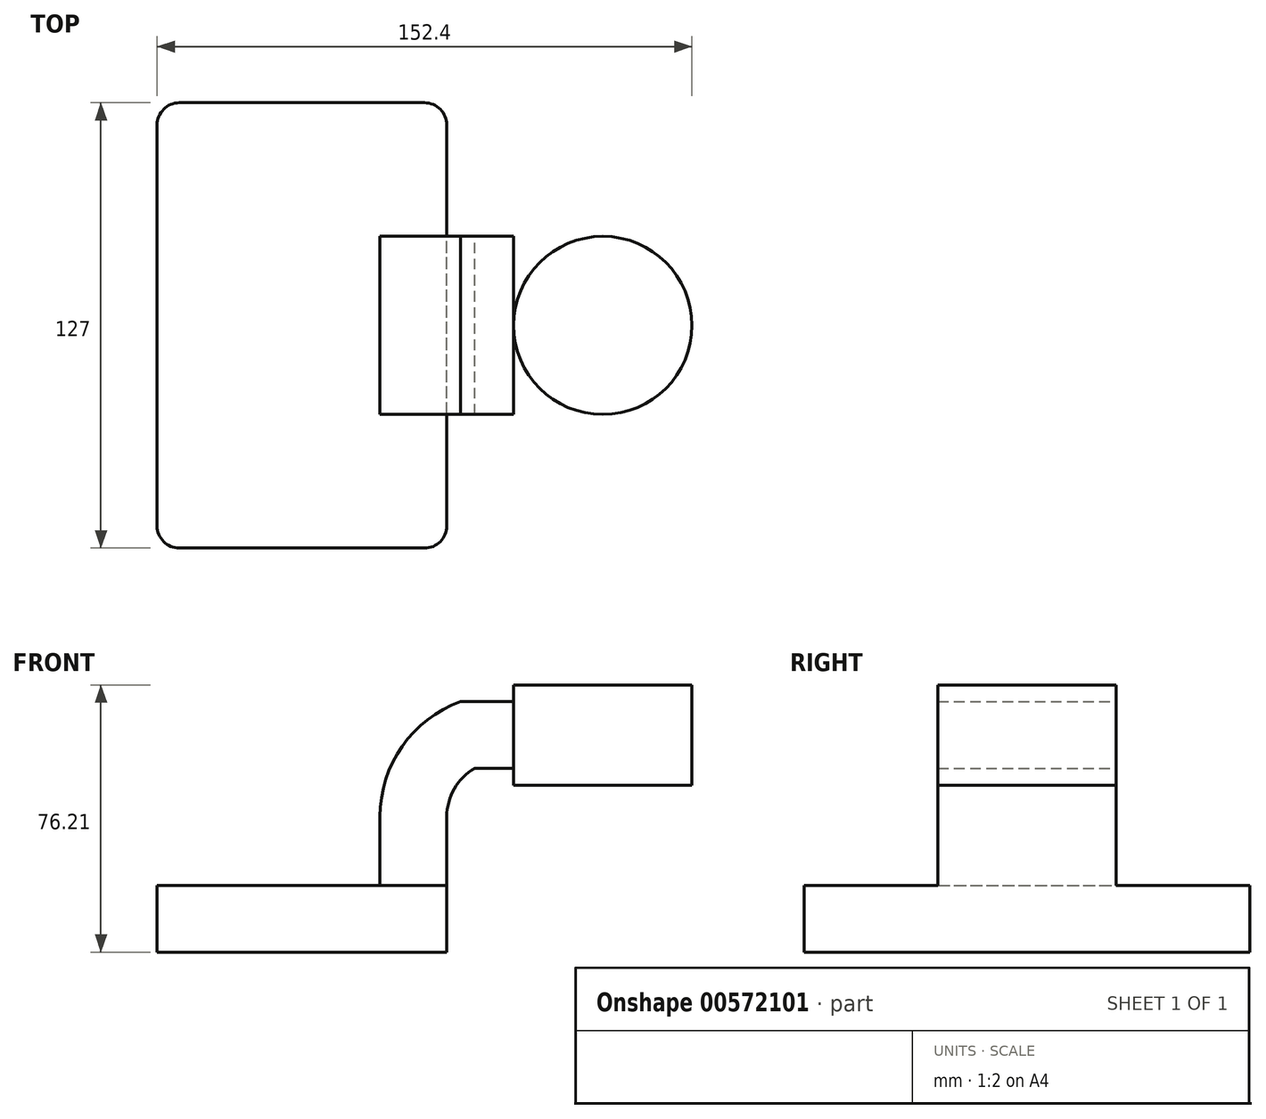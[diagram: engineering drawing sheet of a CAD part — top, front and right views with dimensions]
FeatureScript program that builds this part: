
annotation { "Feature Type Name" : "Feature", "Feature Type Description" : "" }
export const myFeature = defineFeature(function(context is Context, id is Id, definition is map)
    precondition{}
    {
        {
            var Q0;
            Q0=qCreatedBy(makeId("Front.planeOp"),FACE);
            var sketch = newSketch(context, id + "F0", { "sketchPlane" : qUnion([Q0])});
            skLineSegment(sketch, "E0.bottom", {"start": v(41.27, 9.53) * mm, "end": v(-41.28, 9.53) * mm});
            skLineSegment(sketch, "E0.top", {"start": v(41.28, -9.52) * mm, "end": v(-41.27, -9.52) * mm});
            skLineSegment(sketch, "E0.left", {"start": v(41.28, 9.53) * mm, "end": v(41.28, -9.52) * mm});
            skLineSegment(sketch, "E0.right", {"start": v(-41.28, 9.53) * mm, "end": v(-41.27, -9.52) * mm});
            skPoint(sketch, "E0.middle", {"position": v(0, 0) * mm});
            skLineSegment(sketch, "E1.bottom", {"start": v(60.33, 38.1) * mm, "end": v(111.13, 38.1) * mm});
            skLineSegment(sketch, "E1.top", {"start": v(60.33, 66.68) * mm, "end": v(111.12, 66.68) * mm});
            skLineSegment(sketch, "E1.left", {"start": v(60.32, 38.1) * mm, "end": v(60.32, 66.68) * mm});
            skLineSegment(sketch, "E1.right", {"start": v(111.13, 38.1) * mm, "end": v(111.13, 66.68) * mm});
            skPoint(sketch, "E1.middle", {"position": v(85.72, 52.39) * mm});
            skLineSegment(sketch, "E2", {"start": v(41.27, 9.53) * mm, "end": v(41.27, 29.12) * mm});
            skArc(sketch, "E3", {"start": v(41.28, 29.12) * mm, "mid": v(43.4, 37.06) * mm, "end": v(49.22, 42.88) * mm});
            skLineSegment(sketch, "E4", {"start": v(49.22, 42.88) * mm, "end": v(85.72, 42.88) * mm});
            skLineSegment(sketch, "E5.0", {"start": v(45.16, 61.93) * mm, "end": v(85.72, 61.93) * mm});
            skArc(sketch, "E5.1", {"start": v(22.23, 29.12) * mm, "mid": v(28.53, 49.14) * mm, "end": v(45.16, 61.93) * mm});
            skLineSegment(sketch, "E5.2", {"start": v(22.22, 9.53) * mm, "end": v(22.22, 29.12) * mm});
            skLineSegment(sketch, "E6", {"start": v(85.72, 66.68) * mm, "end": v(85.73, 38.1) * mm});
            skFitSpline(sketch, "E7", {"points": [v(-41.28, 9.53) * mm, v(45.16, 61.93) * mm], "startDerivative": vector(0.48, 108.31) * mm, "endDerivative": vector(111.94, 4.14) * mm});
            skSolve(sketch);
        }
        {
            var Q0;
            Q0=makeQuery(id+"F0.imprint","IMPRINT",FACE,{"disambiguationData":[TD([[makeQuery(id+"F0.imprint","IMPRINT",EDGE,{"derivedFrom":sQuery(id+"F0.wireOp",EDGE,"E0.top")}),-1.0]])]});
            extrude(context, id + "F1", {"entities" : qUnion([Q0]), "endBound" : BoundingType.SYMMETRIC, "depth" : 127 * mm, "offsetDistance" : 25.4 * mm});
        }
        {
            var Q0;
            {var subQ1=sQuery(id+"F0.wireOp",EDGE,"E2");Q0=makeQuery(id+"F0.imprint","IMPRINT",FACE,{"disambiguationData":[TD([[makeQuery(id+"F0.imprint","IMPRINT",EDGE,{"derivedFrom":subQ1}),1.0]])]});}
            extrude(context, id + "F2", {"entities" : qUnion([Q0]), "operationType" : NewBodyOperationType.ADD, "endBound" : BoundingType.SYMMETRIC, "depth" : 50.8 * mm, "offsetDistance" : 25.4 * mm});
        }
        {
            var Q0;
            {var subQ0=sQuery(id+"F0.wireOp",EDGE,"E1.right");Q0=makeQuery(id+"F0.imprint","IMPRINT",FACE,{"disambiguationData":[TD([[makeQuery(id+"F0.imprint","IMPRINT",EDGE,{"derivedFrom":subQ0}),1.0]])]});}
            var Q1;
            Q1=sQuery(id+"F0.wireOp",EDGE,"E6");
            revolve(context, id + "F3", {"operationType" : NewBodyOperationType.ADD, "entities" : qUnion([Q0]), "axis" : qUnion([Q1]), "revolveType" : RevolveType.FULL});
        }
        {
            var Q0;
            Q0=makeQuery(id+"F0.imprint","IMPRINT",FACE,{"disambiguationData":[TD([[makeQuery(id+"F0.imprint","IMPRINT",EDGE,{"derivedFrom":sQuery(id+"F0.wireOp",EDGE,"E5.1")}),1.0]])]});
            extrude(context, id + "F4", {"entities" : qUnion([Q0]), "operationType" : NewBodyOperationType.ADD, "endBound" : BoundingType.SYMMETRIC, "depth" : 15.88 * mm, "offsetDistance" : 25.4 * mm});
        }
        {
            var Q0;
            Q0=makeQuery(id+"F1.opExtrude","CAP_EDGE",EDGE,{"disambiguationData":[OSD([sQuery(id+"F0.wireOp",EDGE,"E0.left")])],"isStart":false});
            var Q1;
            Q1=makeQuery(id+"F1.opExtrude","CAP_EDGE",EDGE,{"disambiguationData":[OSD([sQuery(id+"F0.wireOp",EDGE,"E0.right")])],"isStart":false});
            var Q2;
            Q2=makeQuery(id+"F1.opExtrude","CAP_EDGE",EDGE,{"disambiguationData":[OSD([sQuery(id+"F0.wireOp",EDGE,"E0.left")])],"isStart":true});
            var Q3;
            Q3=makeQuery(id+"F1.opExtrude","CAP_EDGE",EDGE,{"disambiguationData":[OSD([sQuery(id+"F0.wireOp",EDGE,"E0.right")])],"isStart":true});
            fillet(context, id + "F5", {"entities" : qUnion([Q0, Q1, Q2, Q3]), "radius" : 6.35 * mm, "tangentPropagation" : true, "allowEdgeOverflow" : false});
        }
    });
